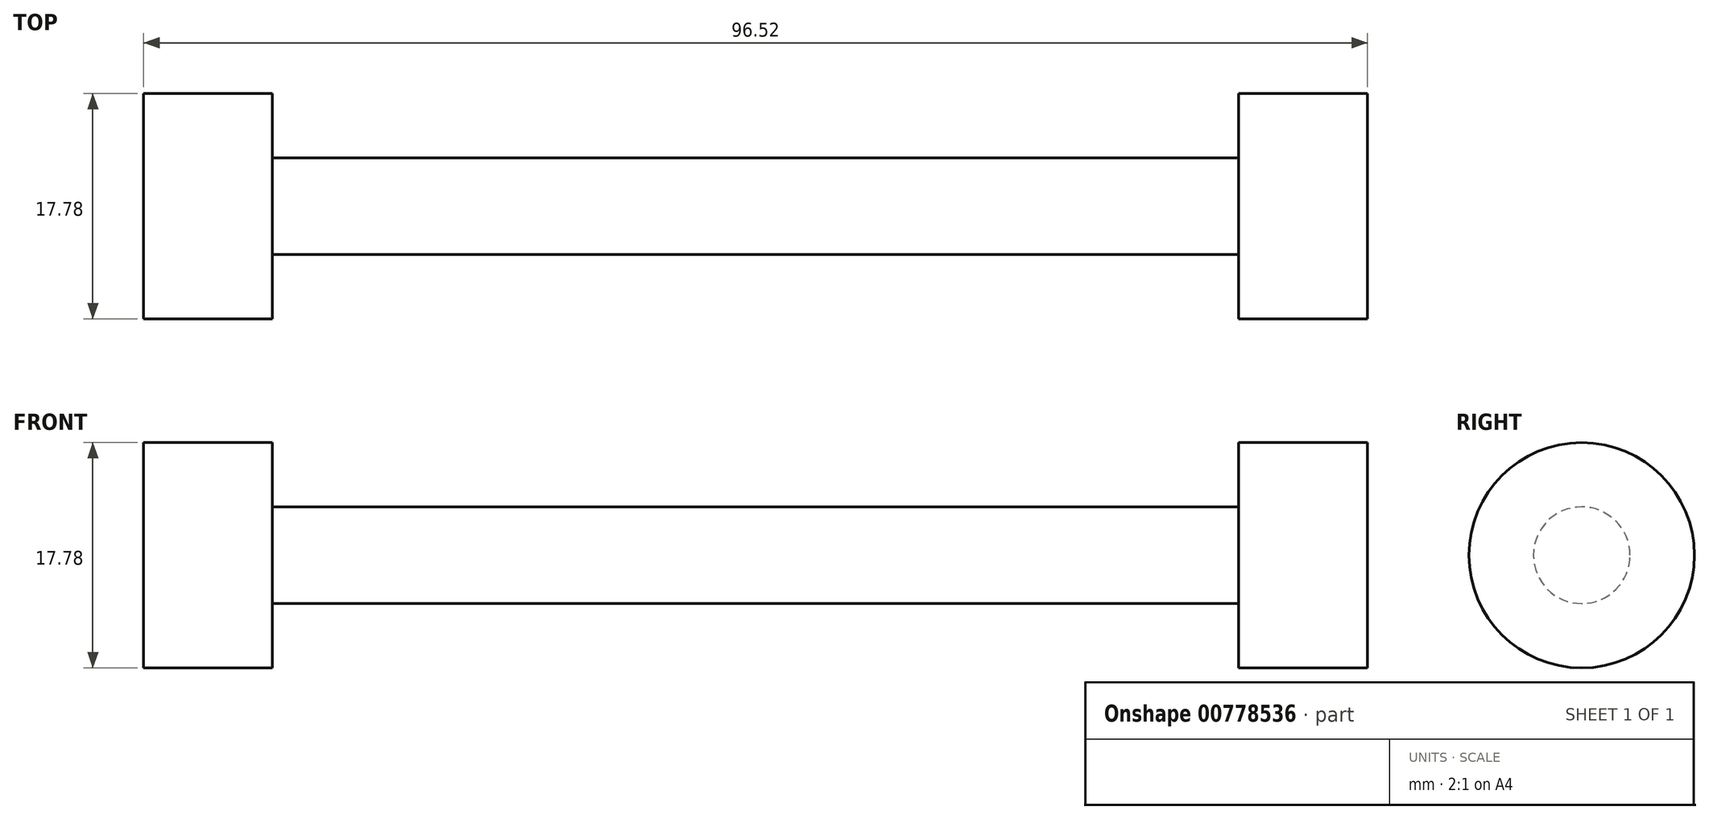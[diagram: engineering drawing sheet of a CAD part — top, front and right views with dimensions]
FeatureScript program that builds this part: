
annotation { "Feature Type Name" : "Feature", "Feature Type Description" : "" }
export const myFeature = defineFeature(function(context is Context, id is Id, definition is map)
    precondition{}
    {
        {
            var Q0;
            Q0=qCreatedBy(makeId("Right.planeOp"),FACE);
            var sketch = newSketch(context, id + "F0", { "sketchPlane" : qUnion([Q0])});
            skCircle(sketch, "E0", {"center": v(0, 0) * mm, "radius": 3.8 * mm});
            skSolve(sketch);
        }
        {
            var Q0;
            Q0 = qSketchRegion(id + "F0", true);
            extrude(context, id + "F1", {"entities" : qUnion([Q0]), "depth" : 76.2 * mm, "offsetDistance" : 25.4 * mm});
        }
        {
            var Q0;
            Q0=makeQuery(id+"F1.opExtrude","CAP_FACE",FACE,{"disambiguationData":[OSD([sQuery(id+"F0.wireOp",EDGE,"E0")])],"isStart":false});
            var sketch = newSketch(context, id + "F2", { "sketchPlane" : qUnion([Q0])});
            skSolve(sketch);
        }
        {
            var Q0;
            Q0=makeQuery(id+"F2.imprint","IMPRINT",FACE,{"disambiguationData":[TD([[makeQuery(id+"F2.imprint","IMPRINT",EDGE,{"derivedFrom":makeQuery(id+"F1.opExtrude","CAP_EDGE",EDGE,{"disambiguationData":[OSD([sQuery(id+"F0.wireOp",EDGE,"E0")])],"isStart":false})}),1.0]])]});
            var sketch = newSketch(context, id + "F3", { "sketchPlane" : qUnion([Q0])});
            skCircle(sketch, "E1", {"center": v(0, 0) * mm, "radius": 8.9 * mm});
            skSolve(sketch);
        }
        {
            var Q0;
            Q0 = qSketchRegion(id + "F3", true);
            extrude(context, id + "F4", {"entities" : qUnion([Q0]), "operationType" : NewBodyOperationType.ADD, "depth" : 10.16 * mm, "offsetDistance" : 25.4 * mm});
        }
        {
            var Q0;
            Q0=makeQuery(id+"F1.opExtrude","CAP_FACE",FACE,{"disambiguationData":[OSD([sQuery(id+"F0.wireOp",EDGE,"E0")])],"isStart":true});
            var sketch = newSketch(context, id + "F5", { "sketchPlane" : qUnion([Q0])});
            skCircle(sketch, "E2", {"center": v(0, 0) * mm, "radius": 8.9 * mm});
            skSolve(sketch);
        }
        {
            var Q0;
            Q0 = qSketchRegion(id + "F5", true);
            extrude(context, id + "F6", {"entities" : qUnion([Q0]), "operationType" : NewBodyOperationType.ADD, "depth" : 10.16 * mm, "offsetDistance" : 25.4 * mm});
        }
    });
